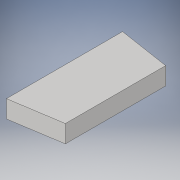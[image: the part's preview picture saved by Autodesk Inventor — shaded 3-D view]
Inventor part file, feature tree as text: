
AUTODESK INVENTOR PART (.ipt)
format: ipt  version: 2018 (Build 220112000, 112)  size: 90,112 bytes
history: native  units: in
note: dims shown in document units (in); Inventor stores cm internally (conversion verified against a paired STEP export)
features: extrude x1, sketch x1
ambient origin geometry x8: Origin, YZ Plane, XZ Plane, XY Plane, X Axis, Y Axis, Z Axis, Center Point
bodies: Solid1 (feature_tree)
feature tree (2):
  extrude  "Extrusion1"  Depth=0.1in
  sketch  "Sketch1"  dims[d0=0.66in d1=0.57in d2=0.29in d3=0.1in d4=0.0in]
